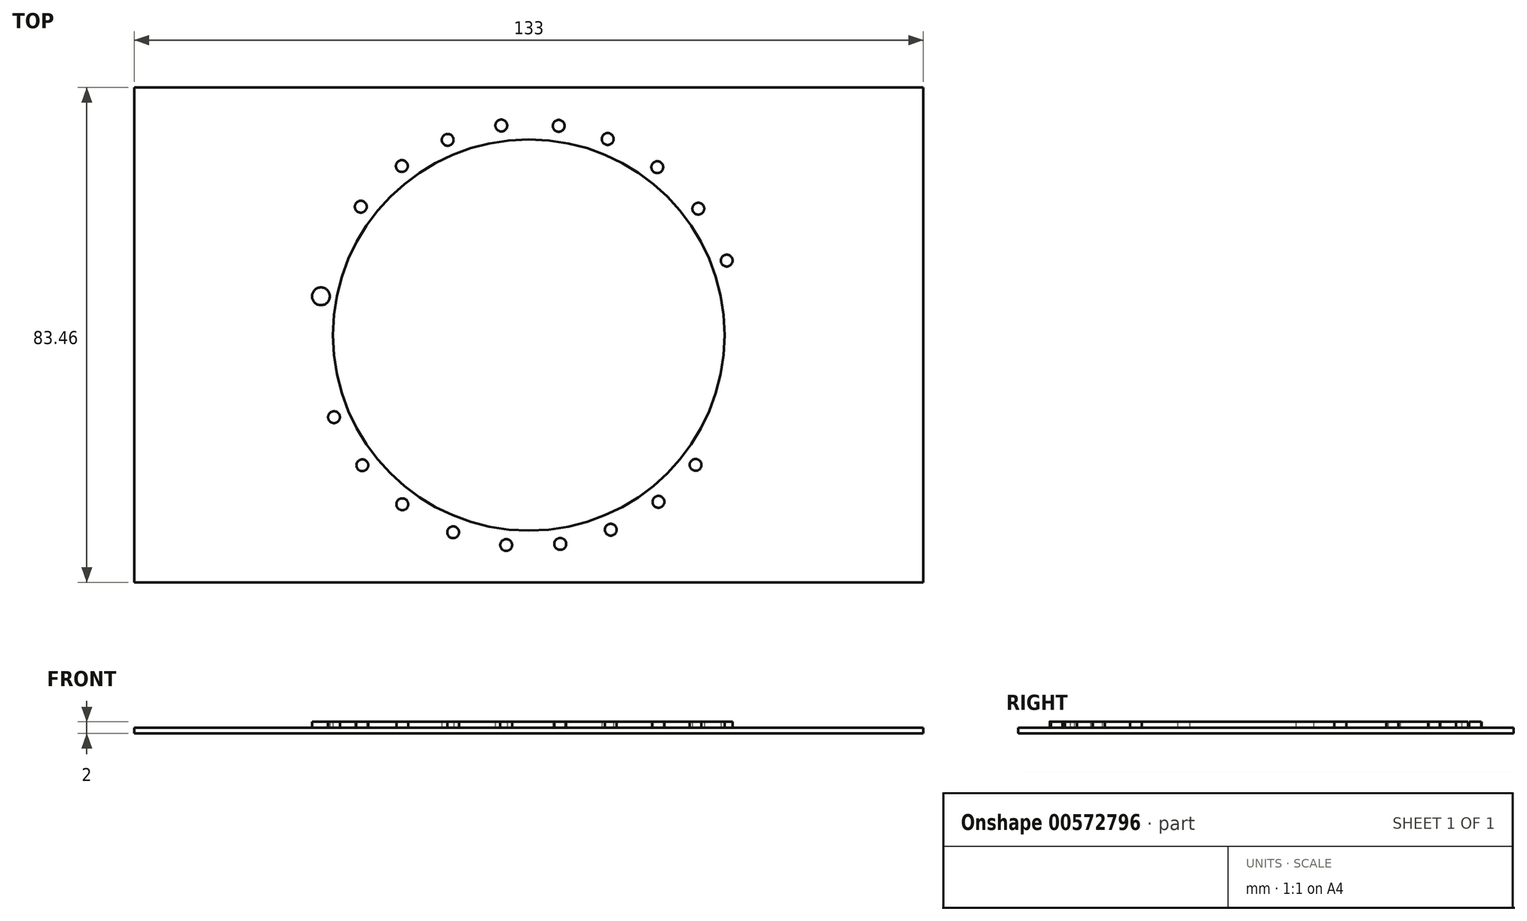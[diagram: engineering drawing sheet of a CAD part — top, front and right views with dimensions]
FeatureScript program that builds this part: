
annotation { "Feature Type Name" : "Feature", "Feature Type Description" : "" }
export const myFeature = defineFeature(function(context is Context, id is Id, definition is map)
    precondition{}
    {
        {
            var Q0;
            Q0=qCreatedBy(makeId("Top.planeOp"),FACE);
            var sketch = newSketch(context, id + "F0", { "sketchPlane" : qUnion([Q0])});
            skCircle(sketch, "E0", {"center": v(0, 0) * mm, "radius": 33 * mm});
            skPoint(sketch, "E1", {"position": v(-13.86, 32.83) * mm});
            skPoint(sketch, "E2", {"position": v(-21.97, 28.06) * mm});
            skPoint(sketch, "E3", {"position": v(-28.56, 21.32) * mm});
            skPoint(sketch, "E4", {"position": v(-33.28, 12.75) * mm});
            skPoint(sketch, "E5", {"position": v(-35.43, 3.81) * mm});
            skPoint(sketch, "E6", {"position": v(-35.24, -5.3) * mm});
            skPoint(sketch, "E7", {"position": v(-32.85, -13.81) * mm});
            skPoint(sketch, "E8", {"position": v(-28.15, -21.86) * mm});
            skPoint(sketch, "E9", {"position": v(-21.91, -28.1) * mm});
            skPoint(sketch, "E10", {"position": v(12.55, -33.36) * mm});
            skPoint(sketch, "E11", {"position": v(21.3, -28.57) * mm});
            skPoint(sketch, "E12", {"position": v(28.3, -21.65) * mm});
            skPoint(sketch, "E13", {"position": v(33.06, -13.3) * mm});
            skPoint(sketch, "E14", {"position": v(35.28, -5.04) * mm});
            skPoint(sketch, "E15", {"position": v(35.34, 4.64) * mm});
            skPoint(sketch, "E16", {"position": v(32.91, 13.67) * mm});
            skPoint(sketch, "E17", {"position": v(28.5, 21.4) * mm});
            skPoint(sketch, "E18", {"position": v(21.64, 28.32) * mm});
            skPoint(sketch, "E19", {"position": v(6.53, 35.04) * mm});
            skCircle(sketch, "E20", {"center": v(0, 0) * mm, "radius": 35.64 * mm, "construction": true});
            skCircle(sketch, "E21", {"center": v(-13.86, 32.83) * mm, "radius": 1 * mm});
            skCircle(sketch, "E22", {"center": v(-21.97, 28.06) * mm, "radius": 1 * mm});
            skCircle(sketch, "E23", {"center": v(-28.56, 21.32) * mm, "radius": 1 * mm});
            skCircle(sketch, "E24", {"center": v(-33.28, 12.75) * mm, "radius": 1 * mm});
            skCircle(sketch, "E25", {"center": v(-35.43, 3.81) * mm, "radius": 1 * mm});
            skCircle(sketch, "E26", {"center": v(-35.24, -5.3) * mm, "radius": 1 * mm});
            skCircle(sketch, "E27", {"center": v(-32.85, -13.81) * mm, "radius": 1 * mm});
            skCircle(sketch, "E28", {"center": v(-28.15, -21.86) * mm, "radius": 1 * mm});
            skCircle(sketch, "E29", {"center": v(-21.91, -28.1) * mm, "radius": 1 * mm});
            skCircle(sketch, "E30", {"center": v(12.55, -33.36) * mm, "radius": 1 * mm});
            skCircle(sketch, "E31", {"center": v(21.3, -28.57) * mm, "radius": 1 * mm});
            skCircle(sketch, "E32", {"center": v(28.3, -21.65) * mm, "radius": 1 * mm});
            skCircle(sketch, "E33", {"center": v(33.06, -13.3) * mm, "radius": 1 * mm});
            skCircle(sketch, "E34", {"center": v(35.28, -5.04) * mm, "radius": 1 * mm});
            skCircle(sketch, "E35", {"center": v(35.34, 4.64) * mm, "radius": 1 * mm});
            skCircle(sketch, "E36", {"center": v(32.91, 13.67) * mm, "radius": 1 * mm});
            skCircle(sketch, "E37", {"center": v(28.5, 21.4) * mm, "radius": 1 * mm});
            skCircle(sketch, "E38", {"center": v(21.64, 28.32) * mm, "radius": 1 * mm});
            skCircle(sketch, "E39", {"center": v(6.53, 35.04) * mm, "radius": 1.5 * mm});
            skLineSegment(sketch, "E40.bottom", {"start": v(-66.5, 41.73) * mm, "end": v(66.5, 41.73) * mm});
            skLineSegment(sketch, "E40.top", {"start": v(-66.5, -41.73) * mm, "end": v(66.5, -41.73) * mm});
            skLineSegment(sketch, "E40.left", {"start": v(-66.5, 41.73) * mm, "end": v(-66.5, -41.73) * mm});
            skLineSegment(sketch, "E40.right", {"start": v(66.5, 41.73) * mm, "end": v(66.5, -41.73) * mm});
            skLineSegment(sketch, "E41.bottom", {"start": v(41.73, -66.5) * mm, "end": v(-41.73, -66.5) * mm});
            skLineSegment(sketch, "E41.top", {"start": v(41.73, 66.5) * mm, "end": v(-41.73, 66.5) * mm});
            skLineSegment(sketch, "E41.left", {"start": v(41.73, -66.5) * mm, "end": v(41.73, 66.5) * mm});
            skLineSegment(sketch, "E41.right", {"start": v(-41.73, -66.5) * mm, "end": v(-41.73, 66.5) * mm});
            skSolve(sketch);
        }
        {
            var Q0;
            {var subQ5=sQuery(id+"F0.wireOp",EDGE,"E41.top");Q0=makeQuery(id+"F0.imprint","IMPRINT",FACE,{"disambiguationData":[TD([[makeQuery(id+"F0.imprint","IMPRINT",EDGE,{"derivedFrom":subQ5}),1.0]])]});}
            var Q1;
            {var subQ5=sQuery(id+"F0.wireOp",EDGE,"E41.bottom");Q1=makeQuery(id+"F0.imprint","IMPRINT",FACE,{"disambiguationData":[TD([[makeQuery(id+"F0.imprint","IMPRINT",EDGE,{"derivedFrom":subQ5}),-1.0]])]});}
            var Q2;
            Q2=makeQuery(id+"F0.imprint","IMPRINT",FACE,{"disambiguationData":[TD([[makeQuery(id+"F0.imprint","IMPRINT",EDGE,{"derivedFrom":sQuery(id+"F0.wireOp",EDGE,"E0")}),-1.0]])]});
            extrude(context, id + "F1", {"entities" : qUnion([Q0, Q1, Q2]), "depth" : 1 * mm, "offsetDistance" : 25 * mm});
        }
        {
            var Q0;
            Q0=makeQuery(id+"F0.imprint","IMPRINT",FACE,{"disambiguationData":[TD([[makeQuery(id+"F0.imprint","IMPRINT",EDGE,{"derivedFrom":sQuery(id+"F0.wireOp",EDGE,"E0")}),1.0]])]});
            var Q1;
            Q1=makeQuery(id+"F0.imprint","IMPRINT",FACE,{"disambiguationData":[TD([[makeQuery(id+"F0.imprint","IMPRINT",EDGE,{"derivedFrom":sQuery(id+"F0.wireOp",EDGE,"E21")}),1.0]])]});
            var Q2;
            Q2=makeQuery(id+"F0.imprint","IMPRINT",FACE,{"disambiguationData":[TD([[makeQuery(id+"F0.imprint","IMPRINT",EDGE,{"derivedFrom":sQuery(id+"F0.wireOp",EDGE,"E22")}),1.0]])]});
            var Q3;
            Q3=makeQuery(id+"F0.imprint","IMPRINT",FACE,{"disambiguationData":[TD([[makeQuery(id+"F0.imprint","IMPRINT",EDGE,{"derivedFrom":sQuery(id+"F0.wireOp",EDGE,"E23")}),1.0]])]});
            var Q4;
            Q4=makeQuery(id+"F0.imprint","IMPRINT",FACE,{"disambiguationData":[TD([[makeQuery(id+"F0.imprint","IMPRINT",EDGE,{"derivedFrom":sQuery(id+"F0.wireOp",EDGE,"E24")}),1.0]])]});
            var Q5;
            Q5=makeQuery(id+"F0.imprint","IMPRINT",FACE,{"disambiguationData":[TD([[makeQuery(id+"F0.imprint","IMPRINT",EDGE,{"derivedFrom":sQuery(id+"F0.wireOp",EDGE,"E25")}),1.0]])]});
            var Q6;
            Q6=makeQuery(id+"F0.imprint","IMPRINT",FACE,{"disambiguationData":[TD([[makeQuery(id+"F0.imprint","IMPRINT",EDGE,{"derivedFrom":sQuery(id+"F0.wireOp",EDGE,"E26")}),1.0]])]});
            var Q7;
            Q7=makeQuery(id+"F0.imprint","IMPRINT",FACE,{"disambiguationData":[TD([[makeQuery(id+"F0.imprint","IMPRINT",EDGE,{"derivedFrom":sQuery(id+"F0.wireOp",EDGE,"E27")}),1.0]])]});
            var Q8;
            Q8=makeQuery(id+"F0.imprint","IMPRINT",FACE,{"disambiguationData":[TD([[makeQuery(id+"F0.imprint","IMPRINT",EDGE,{"derivedFrom":sQuery(id+"F0.wireOp",EDGE,"E28")}),1.0]])]});
            var Q9;
            Q9=makeQuery(id+"F0.imprint","IMPRINT",FACE,{"disambiguationData":[TD([[makeQuery(id+"F0.imprint","IMPRINT",EDGE,{"derivedFrom":sQuery(id+"F0.wireOp",EDGE,"E29")}),1.0]])]});
            var Q10;
            Q10=makeQuery(id+"F0.imprint","IMPRINT",FACE,{"disambiguationData":[TD([[makeQuery(id+"F0.imprint","IMPRINT",EDGE,{"derivedFrom":sQuery(id+"F0.wireOp",EDGE,"E30")}),1.0]])]});
            var Q11;
            Q11=makeQuery(id+"F0.imprint","IMPRINT",FACE,{"disambiguationData":[TD([[makeQuery(id+"F0.imprint","IMPRINT",EDGE,{"derivedFrom":sQuery(id+"F0.wireOp",EDGE,"E31")}),1.0]])]});
            var Q12;
            Q12=makeQuery(id+"F0.imprint","IMPRINT",FACE,{"disambiguationData":[TD([[makeQuery(id+"F0.imprint","IMPRINT",EDGE,{"derivedFrom":sQuery(id+"F0.wireOp",EDGE,"E32")}),1.0]])]});
            var Q13;
            Q13=makeQuery(id+"F0.imprint","IMPRINT",FACE,{"disambiguationData":[TD([[makeQuery(id+"F0.imprint","IMPRINT",EDGE,{"derivedFrom":sQuery(id+"F0.wireOp",EDGE,"E33")}),1.0]])]});
            var Q14;
            Q14=makeQuery(id+"F0.imprint","IMPRINT",FACE,{"disambiguationData":[TD([[makeQuery(id+"F0.imprint","IMPRINT",EDGE,{"derivedFrom":sQuery(id+"F0.wireOp",EDGE,"E34")}),1.0]])]});
            var Q15;
            Q15=makeQuery(id+"F0.imprint","IMPRINT",FACE,{"disambiguationData":[TD([[makeQuery(id+"F0.imprint","IMPRINT",EDGE,{"derivedFrom":sQuery(id+"F0.wireOp",EDGE,"E35")}),1.0]])]});
            var Q16;
            Q16=makeQuery(id+"F0.imprint","IMPRINT",FACE,{"disambiguationData":[TD([[makeQuery(id+"F0.imprint","IMPRINT",EDGE,{"derivedFrom":sQuery(id+"F0.wireOp",EDGE,"E36")}),1.0]])]});
            var Q17;
            Q17=makeQuery(id+"F0.imprint","IMPRINT",FACE,{"disambiguationData":[TD([[makeQuery(id+"F0.imprint","IMPRINT",EDGE,{"derivedFrom":sQuery(id+"F0.wireOp",EDGE,"E37")}),1.0]])]});
            var Q18;
            Q18=makeQuery(id+"F0.imprint","IMPRINT",FACE,{"disambiguationData":[TD([[makeQuery(id+"F0.imprint","IMPRINT",EDGE,{"derivedFrom":sQuery(id+"F0.wireOp",EDGE,"E38")}),1.0]])]});
            var Q19;
            Q19=makeQuery(id+"F0.imprint","IMPRINT",FACE,{"disambiguationData":[TD([[makeQuery(id+"F0.imprint","IMPRINT",EDGE,{"derivedFrom":sQuery(id+"F0.wireOp",EDGE,"E39")}),1.0]])]});
            extrude(context, id + "F2", {"entities" : qUnion([Q0, Q1, Q2, Q3, Q4, Q5, Q6, Q7, Q8, Q9, Q10, Q11, Q12, Q13, Q14, Q15, Q16, Q17, Q18, Q19]), "operationType" : NewBodyOperationType.ADD, "depth" : 2 * mm, "offsetDistance" : 25 * mm});
        }
        {
            var Q0;
            Q0=makeQuery(id+"F1.opExtrude","SWEPT_BODY",BODY,{"disambiguationData":[OSD([sQuery(id+"F0.wireOp",EDGE,"E0"),sQuery(id+"F0.wireOp",EDGE,"E21"),sQuery(id+"F0.wireOp",EDGE,"E22"),sQuery(id+"F0.wireOp",EDGE,"E23"),sQuery(id+"F0.wireOp",EDGE,"E24"),sQuery(id+"F0.wireOp",EDGE,"E25"),sQuery(id+"F0.wireOp",EDGE,"E26"),sQuery(id+"F0.wireOp",EDGE,"E27"),sQuery(id+"F0.wireOp",EDGE,"E28"),sQuery(id+"F0.wireOp",EDGE,"E29"),sQuery(id+"F0.wireOp",EDGE,"E30"),sQuery(id+"F0.wireOp",EDGE,"E31"),sQuery(id+"F0.wireOp",EDGE,"E32"),sQuery(id+"F0.wireOp",EDGE,"E33"),sQuery(id+"F0.wireOp",EDGE,"E34"),sQuery(id+"F0.wireOp",EDGE,"E35"),sQuery(id+"F0.wireOp",EDGE,"E36"),sQuery(id+"F0.wireOp",EDGE,"E37"),sQuery(id+"F0.wireOp",EDGE,"E38"),sQuery(id+"F0.wireOp",EDGE,"E39"),sQuery(id+"F0.wireOp",EDGE,"E41.bottom"),sQuery(id+"F0.wireOp",EDGE,"E41.top"),sQuery(id+"F0.wireOp",EDGE,"E41.left"),sQuery(id+"F0.wireOp",EDGE,"E41.right")])]});
            var Q1;
            Q1=makeQuery(id+"F2.opExtrude","CAP_EDGE",EDGE,{"disambiguationData":[OSD([sQuery(id+"F0.wireOp",EDGE,"E0")])],"isStart":false});
            transform(context, id + "F3", {"entities" : qUnion([Q0]), "transformType" : TransformType.ROTATION, "transformAxis" : qUnion([Q1]), "angle" : 90 * degree, "makeCopy" : false});
        }
    });
